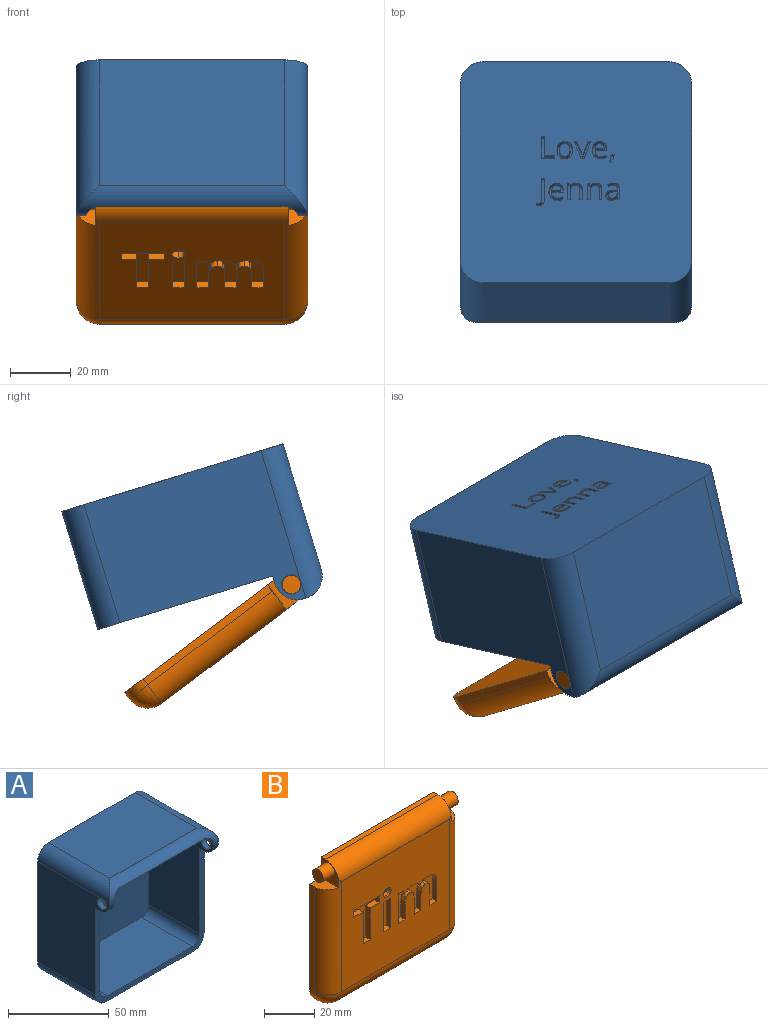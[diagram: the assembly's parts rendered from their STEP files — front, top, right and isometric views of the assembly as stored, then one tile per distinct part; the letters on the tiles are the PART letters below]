
ASSEMBLY  parts=2 mates=1
PART A: 195 faces, bbox 76.2x50.8x76.2 mm
  f0: plane 76.2x76.2mm, normal (0,1,0), area 5627.7mm2, adj f2,f6,f10,f11,f19,f21,f22,f23
  f1: plane 3.22x0.71mm, normal (0,-1,0), area 2.3mm2, adj f2,f3,f17,f20,f29
  f2: plane 60.96x50.8mm, normal (1,0,0), area 2517.9mm2, adj f0,f1,f12,f14,f16,f17,f19,f23
  f3: plane 59.69x45.72mm, normal (-1,0,0), area 2158mm2, adj f1,f8,f12,f14,f16,f17,f28,f29
  f4: plane 59.69x35.56mm, normal (0,0,1), area 2122.6mm2, adj f8,f16,f27,f28
  f5: plane 3.22x0.71mm, normal (0,-1,0), area 2.3mm2, adj f6,f7,f18,f20,f24
  f6: plane 60.96x50.8mm, normal (-1,0,0), area 2517.9mm2, adj f0,f5,f13,f15,f16,f18,f21,f22
  f7: plane 59.69x45.72mm, normal (1,0,0), area 2158mm2, adj f5,f8,f13,f15,f16,f18,f24,f26
  f8: plane 69.85x69.85mm, normal (0,-1,0), area 4856.9mm2, adj f3,f4,f7,f9,f26,f27,f28,f31
  f9: plane 59.75x44.29mm, normal (0,0,-1), area 2643.7mm2, adj f8,f20,f24,f25,f26,f29,f30,f31
  f10: plane 60.96x40.64mm, normal (0,0,-1), area 2477.4mm2, adj f0,f16,f22,f23
  f11: plane 60.96x43.18mm, normal (0,0,1), area 2632.3mm2, adj f0,f19,f20,f21
  f12: cylinder r=3.17mm len=6.35mm, axis (1,0,0), area 63.3mm2, adj f2,f3,f30
  f13: cylinder r=3.17mm len=6.35mm, axis (-1,0,0), area 63.3mm2, adj f6,f7,f25
  f14: plane 3.18x2.54mm, normal (0,0,-1), area 8.1mm2, adj f2,f3,f16,f17
  f15: plane 3.18x2.54mm, normal (0,0,-1), area 8.1mm2, adj f6,f7,f16,f18
  f16: plane 76.2x60.25mm, normal (0,-1,0), area 590.5mm2, adj f2,f3,f4,f6,f7,f10,f14,f15
  f17: cylinder r=7.62mm len=7.62mm, axis (1,0,0), area 38mm2, adj f1,f2,f3,f14
  f18: cylinder r=7.62mm len=7.62mm, axis (1,0,0), area 38mm2, adj f5,f6,f7,f15
  f19: cylinder r=7.62mm len=50.8mm, axis (0,-1,0), area 574.9mm2, adj f0,f2,f11,f20
  f20: cylinder r=7.62mm len=76.2mm, axis (1,0,0), area 526.7mm2, adj f1,f5,f9,f11,f19,f21,f24,f29
  f21: cylinder r=7.62mm len=50.8mm, axis (0,-1,0), area 574.9mm2, adj f0,f6,f11,f20
  f22: cylinder r=7.62mm len=40.64mm, axis (0,1,0), area 486.4mm2, adj f0,f6,f10,f16
  f23: cylinder r=7.62mm len=40.64mm, axis (0,1,0), area 486.4mm2, adj f0,f2,f10,f16
  f24: cylinder r=5.08mm len=5.08mm, axis (0,1,0), area 26.1mm2, adj f5,f7,f9,f20,f25
  f25: bspline ~5.08x5.08mm, area 27.4mm2, adj f9,f13,f24,f26
  f26: cylinder r=5.08mm len=38.19mm, axis (0,1,0), area 304.7mm2, adj f7,f8,f9,f25
  f27: cylinder r=5.08mm len=35.56mm, axis (0,-1,0), area 283.8mm2, adj f4,f7,f8,f16
  f28: cylinder r=5.08mm len=35.56mm, axis (0,-1,0), area 283.8mm2, adj f3,f4,f8,f16
  f29: cylinder r=5.08mm len=5.08mm, axis (0,1,0), area 26.1mm2, adj f1,f3,f9,f20,f30
  f30: bspline ~5.08x5.08mm, area 27.4mm2, adj f9,f12,f29,f31
  f31: cylinder r=5.08mm len=38.19mm, axis (0,1,0), area 304.7mm2, adj f3,f8,f9,f30
  f32: plane 7.54x2.54mm, normal (1,0,0), area 19.1mm2, adj f0,f33,f37,f38
  f33: plane 4.2x2.54mm, normal (0,0,-1), area 10.7mm2, adj f0,f32,f34,f38
  f34: plane 2.54x0.79mm, normal (-1,0,0), area 2mm2, adj f0,f33,f35,f38
  f35: plane 3.33x2.54mm, normal (0,0,1), area 8.4mm2, adj f0,f34,f36,f38
  f36: plane 6.74x2.54mm, normal (-1,0,0), area 17.1mm2, adj f0,f35,f37,f38
  f37: plane 2.54x0.88mm, normal (0,0,1), area 2.2mm2, adj f0,f32,f36,f38
  f38: plane 7.54x4.2mm, normal (0,1,0), area 9.2mm2, adj f32,f33,f34,f35,f36,f37
  f39: extruded ~2.54x1.26mm, area 3.5mm2, adj f40,f65,f66,f191
  f40: extruded ~2.54x0.79mm, area 2.1mm2, adj f39,f41,f66,f191
  f41: extruded ~2.54x0.71mm, area 2mm2, adj f40,f42,f66,f191
  f42: extruded ~2.54x0.87mm, area 2.6mm2, adj f41,f43,f66,f191
  f43: extruded ~2.54x1.47mm, area 3.9mm2, adj f42,f44,f66,f191
  f44: plane 2.54x0.86mm, normal (-0.04,0,-1), area 2.2mm2, adj f43,f45,f66,f191
  f45: plane 2.54x0.51mm, normal (1,0,0), area 1.3mm2, adj f44,f65,f66,f191
  f46: plane 2.54x0.81mm, normal (0.98,0,-0.21), area 2.1mm2, adj f0,f47,f64,f66
  f47: plane 2.54x0.64mm, normal (0,0,-1), area 1.6mm2, adj f0,f46,f48,f66
  f48: plane 3.86x2.54mm, normal (-1,0,0), area 9.8mm2, adj f0,f47,f49,f66
  f49: extruded ~2.54x1.44mm, area 4mm2, adj f0,f48,f50,f66
  f50: extruded ~2.54x1.5mm, area 4.1mm2, adj f0,f49,f51,f66
  f51: extruded ~2.54x1mm, area 2.6mm2, adj f0,f50,f52,f66
  f52: extruded ~2.54x0.91mm, area 2.5mm2, adj f0,f51,f53,f66
  f53: plane 2.54x0.65mm, normal (0.93,0,-0.37), area 1.8mm2, adj f0,f52,f54,f66
  f54: extruded ~2.54x1.6mm, area 4.2mm2, adj f0,f53,f55,f66
  f55: extruded ~2.54x0.92mm, area 2.5mm2, adj f0,f54,f56,f66
  f56: extruded ~2.54x0.98mm, area 2.7mm2, adj f0,f55,f57,f66
  f57: plane 2.54x0.35mm, normal (1,0,0), area 0.9mm2, adj f0,f56,f58,f66
  f58: plane 2.54x0.96mm, normal (0.03,0,1), area 2.4mm2, adj f0,f57,f59,f66
  f59: extruded ~2.74x2.54mm, area 9.3mm2, adj f0,f58,f60,f66
  f60: extruded ~2.54x1.23mm, area 3.5mm2, adj f0,f59,f61,f66
  f61: extruded ~2.54x1.32mm, area 3.6mm2, adj f0,f60,f62,f66
  f62: extruded ~2.54x1.05mm, area 2.7mm2, adj f0,f61,f63,f66
  f63: extruded ~2.54x0.84mm, area 2.8mm2, adj f0,f62,f64,f66
  f64: plane 2.54x0.04mm, normal (0,0,-1), area 0.1mm2, adj f0,f46,f63,f66
  f65: extruded ~2.54x1.23mm, area 3.4mm2, adj f39,f45,f66,f191
  f66: plane 5.85x4.53mm, normal (0,1,0), area 12.5mm2, adj f39,f40,f41,f42,f43,f44,f45,f46
  f67: plane 5.65x2.54mm, normal (0.93,0,-0.35), area 15.3mm2, adj f0,f68,f76,f77
  f68: plane 2.54x1mm, normal (0,0,-1), area 2.5mm2, adj f0,f67,f69,f77
  f69: plane 5.65x2.54mm, normal (-0.93,0,-0.35), area 15.3mm2, adj f0,f68,f70,f77
  f70: plane 2.54x0.92mm, normal (0,0,1), area 2.3mm2, adj f0,f69,f71,f77
  f71: extruded ~3.75x2.54mm, area 10.1mm2, adj f0,f70,f72,f77
  f72: extruded ~2.54x1.13mm, area 3mm2, adj f0,f71,f73,f77
  f73: plane 2.54x0.04mm, normal (0,0,1), area 0.1mm2, adj f0,f72,f74,f77
  f74: extruded ~2.54x1.53mm, area 4.1mm2, adj f0,f73,f75,f77
  f75: plane 3.35x2.54mm, normal (-0.94,0,0.34), area 9.1mm2, adj f0,f74,f76,f77
  f76: plane 2.54x0.92mm, normal (0,0,1), area 2.3mm2, adj f0,f67,f75,f77
  f77: plane 5.65x5.29mm, normal (0,1,0), area 9.5mm2, adj f67,f68,f69,f70,f71,f72,f73,f74
  f78: plane 2.54x0.12mm, normal (-0.84,0,0.55), area 0.4mm2, adj f0,f79,f84,f85
  f79: plane 2.54x0.94mm, normal (0,0,1), area 2.4mm2, adj f0,f78,f80,f85
  f80: extruded ~2.54x1.26mm, area 3.3mm2, adj f0,f79,f81,f85
  f81: extruded ~2.54x1.32mm, area 3.5mm2, adj f0,f80,f82,f85
  f82: plane 2.54x0.65mm, normal (0,0,-1), area 1.6mm2, adj f0,f81,f83,f85
  f83: extruded ~2.54x1.27mm, area 3.5mm2, adj f0,f82,f84,f85
  f84: extruded ~2.54x1.2mm, area 3.2mm2, adj f0,f78,f83,f85
  f85: plane 2.59x1.56mm, normal (0,1,0), area 2.2mm2, adj f78,f79,f80,f81,f82,f83,f84
  f86: extruded ~2.54x0.76mm, area 2mm2, adj f0,f87,f95,f96
  f87: extruded ~2.54x1.42mm, area 4mm2, adj f0,f86,f88,f96
  f88: extruded ~2.54x1.52mm, area 4.2mm2, adj f0,f87,f89,f96
  f89: plane 7.46x2.54mm, normal (-1,0,0), area 19mm2, adj f0,f88,f90,f96
  f90: plane 2.54x0.88mm, normal (0,0,1), area 2.2mm2, adj f0,f89,f91,f96
  f91: plane 7.54x2.54mm, normal (1,0,0), area 19.1mm2, adj f0,f90,f92,f96
  f92: extruded ~2.54x0.89mm, area 2.4mm2, adj f0,f91,f93,f96
  f93: extruded ~2.54x0.78mm, area 2.2mm2, adj f0,f92,f94,f96
  f94: extruded ~2.54x0.76mm, area 2mm2, adj f0,f93,f95,f96
  f95: plane 2.54x0.75mm, normal (1,0,0), area 1.9mm2, adj f0,f86,f94,f96
  f96: plane 9.52x2.68mm, normal (0,1,0), area 9.3mm2, adj f86,f87,f88,f89,f90,f91,f92,f93
  f97: plane 3.66x2.54mm, normal (1,0,0), area 9.3mm2, adj f0,f98,f113,f114
  f98: plane 2.54x0.86mm, normal (0,0,-1), area 2.2mm2, adj f0,f97,f99,f114
  f99: plane 3.68x2.54mm, normal (-1,0,0), area 9.4mm2, adj f0,f98,f100,f114
  f100: extruded ~2.54x1.58mm, area 4.3mm2, adj f0,f99,f101,f114
  f101: extruded ~2.54x1.54mm, area 4.2mm2, adj f0,f100,f102,f114
  f102: extruded ~2.54x1.06mm, area 2.8mm2, adj f0,f101,f103,f114
  f103: extruded ~2.54x0.74mm, area 2.5mm2, adj f0,f102,f104,f114
  f104: plane 2.54x0.04mm, normal (0,0,1), area 0.1mm2, adj f0,f103,f105,f114
  f105: plane 2.54x0.77mm, normal (-0.98,0,0.18), area 2mm2, adj f0,f104,f106,f114
  f106: plane 2.54x0.7mm, normal (0,0,1), area 1.8mm2, adj f0,f105,f107,f114
  f107: plane 5.65x2.54mm, normal (1,0,0), area 14.3mm2, adj f0,f106,f108,f114
  f108: plane 2.54x0.86mm, normal (0,0,-1), area 2.2mm2, adj f0,f107,f109,f114
  f109: plane 2.96x2.54mm, normal (-1,0,0), area 7.5mm2, adj f0,f108,f110,f114
  f110: extruded ~2.54x1.58mm, area 4.2mm2, adj f0,f109,f111,f114
  f111: extruded ~2.54x1.3mm, area 3.6mm2, adj f0,f110,f112,f114
  f112: extruded ~2.54x0.99mm, area 2.7mm2, adj f0,f111,f113,f114
  f113: extruded ~2.54x1.03mm, area 2.8mm2, adj f0,f97,f112,f114
  f114: plane 5.75x4.72mm, normal (0,1,0), area 11.6mm2, adj f97,f98,f99,f100,f101,f102,f103,f104
  f115: extruded ~2.54x1.08mm, area 3.1mm2, adj f116,f133,f134,f192
  f116: extruded ~2.54x1.03mm, area 2.9mm2, adj f115,f117,f134,f192
  f117: extruded ~2.54x1.24mm, area 3.3mm2, adj f116,f118,f134,f192
  f118: plane 2.95x2.54mm, normal (0,0,1), area 7.5mm2, adj f117,f133,f134,f192
  f119: extruded ~2.54x1.98mm, area 5.5mm2, adj f0,f120,f132,f134
  f120: extruded ~2.54x0.98mm, area 2.5mm2, adj f0,f119,f121,f134
  f121: extruded ~2.54x0.86mm, area 2.3mm2, adj f0,f120,f122,f134
  f122: plane 2.54x0.76mm, normal (-1,0,0), area 1.9mm2, adj f0,f121,f123,f134
  f123: extruded ~2.54x1.8mm, area 4.7mm2, adj f0,f122,f124,f134
  f124: extruded ~2.54x1.34mm, area 3.8mm2, adj f0,f123,f125,f134
  f125: extruded ~2.54x1.51mm, area 4.1mm2, adj f0,f124,f126,f134
  f126: plane 3.89x2.54mm, normal (0,0,-1), area 9.9mm2, adj f0,f125,f127,f134
  f127: plane 2.54x0.54mm, normal (-1,0,0), area 1.4mm2, adj f0,f126,f128,f134
  f128: extruded ~2.54x1.84mm, area 5.1mm2, adj f0,f127,f129,f134
  f129: extruded ~2.54x1.68mm, area 4.8mm2, adj f0,f128,f130,f134
  f130: extruded ~2.54x1.81mm, area 5.2mm2, adj f0,f129,f131,f134
  f131: extruded ~2.54x2.17mm, area 5.9mm2, adj f0,f130,f132,f134
  f132: extruded ~2.54x2.12mm, area 5.8mm2, adj f0,f119,f131,f134
  f133: extruded ~2.54x1.23mm, area 3.4mm2, adj f115,f118,f134,f192
  f134: plane 5.86x4.78mm, normal (0,1,0), area 12.7mm2, adj f115,f116,f117,f118,f119,f120,f121,f122
  f135: extruded ~2.54x1.08mm, area 3.1mm2, adj f136,f153,f154,f193
  f136: extruded ~2.54x1.03mm, area 2.9mm2, adj f135,f137,f154,f193
  f137: extruded ~2.54x1.24mm, area 3.3mm2, adj f136,f138,f154,f193
  f138: plane 2.95x2.54mm, normal (0,0,1), area 7.5mm2, adj f137,f153,f154,f193
  f139: extruded ~2.54x1.98mm, area 5.5mm2, adj f0,f140,f152,f154
  f140: extruded ~2.54x0.98mm, area 2.5mm2, adj f0,f139,f141,f154
  f141: extruded ~2.54x0.86mm, area 2.3mm2, adj f0,f140,f142,f154
  f142: plane 2.54x0.76mm, normal (-1,0,0), area 1.9mm2, adj f0,f141,f143,f154
  f143: extruded ~2.54x1.8mm, area 4.7mm2, adj f0,f142,f144,f154
  f144: extruded ~2.54x1.34mm, area 3.8mm2, adj f0,f143,f145,f154
  f145: extruded ~2.54x1.51mm, area 4.1mm2, adj f0,f144,f146,f154
  f146: plane 3.89x2.54mm, normal (0,0,-1), area 9.9mm2, adj f0,f145,f147,f154
  f147: plane 2.54x0.54mm, normal (-1,0,0), area 1.4mm2, adj f0,f146,f148,f154
  f148: extruded ~2.54x1.84mm, area 5.1mm2, adj f0,f147,f149,f154
  f149: extruded ~2.54x1.68mm, area 4.8mm2, adj f0,f148,f150,f154
  f150: extruded ~2.54x1.81mm, area 5.2mm2, adj f0,f149,f151,f154
  f151: extruded ~2.54x2.17mm, area 5.9mm2, adj f0,f150,f152,f154
  f152: extruded ~2.54x2.12mm, area 5.8mm2, adj f0,f139,f151,f154
  f153: extruded ~2.54x1.23mm, area 3.4mm2, adj f135,f138,f154,f193
  f154: plane 5.86x4.78mm, normal (0,1,0), area 12.7mm2, adj f135,f136,f137,f138,f139,f140,f141,f142
  f155: extruded ~2.54x1.65mm, area 4.4mm2, adj f156,f171,f172,f194
  f156: extruded ~2.54x1.64mm, area 4.4mm2, adj f155,f157,f172,f194
  f157: extruded ~2.54x1.27mm, area 3.6mm2, adj f156,f158,f172,f194
  f158: extruded ~2.54x1.29mm, area 3.7mm2, adj f157,f159,f172,f194
  f159: extruded ~2.54x1.64mm, area 4.4mm2, adj f158,f160,f172,f194
  f160: extruded ~2.54x1.65mm, area 4.4mm2, adj f159,f161,f172,f194
  f161: extruded ~2.54x1.28mm, area 3.7mm2, adj f160,f171,f172,f194
  f162: extruded ~2.54x2.16mm, area 5.9mm2, adj f0,f163,f170,f172
  f163: extruded ~2.54x2.13mm, area 5.8mm2, adj f0,f162,f164,f172
  f164: extruded ~2.54x1.88mm, area 5.4mm2, adj f0,f163,f165,f172
  f165: extruded ~2.54x1.92mm, area 5.4mm2, adj f0,f164,f166,f172
  f166: extruded ~2.54x2.15mm, area 5.9mm2, adj f0,f165,f167,f172
  f167: extruded ~2.54x1.56mm, area 4.1mm2, adj f0,f166,f168,f172
  f168: extruded ~2.54x1.02mm, area 3.5mm2, adj f0,f167,f169,f172
  f169: extruded ~2.54x1.35mm, area 3.6mm2, adj f0,f168,f170,f172
  f170: extruded ~2.54x1.92mm, area 5.4mm2, adj f0,f162,f169,f172
  f171: extruded ~2.54x1.27mm, area 3.7mm2, adj f155,f161,f172,f194
  f172: plane 5.86x5.19mm, normal (0,1,0), area 12.3mm2, adj f155,f156,f157,f158,f159,f160,f161,f162
  f173: plane 3.66x2.54mm, normal (1,0,0), area 9.3mm2, adj f0,f174,f189,f190
  f174: plane 2.54x0.86mm, normal (0,0,-1), area 2.2mm2, adj f0,f173,f175,f190
  f175: plane 3.68x2.54mm, normal (-1,0,0), area 9.4mm2, adj f0,f174,f176,f190
  f176: extruded ~2.54x1.58mm, area 4.3mm2, adj f0,f175,f177,f190
  f177: extruded ~2.54x1.54mm, area 4.2mm2, adj f0,f176,f178,f190
  f178: extruded ~2.54x1.06mm, area 2.8mm2, adj f0,f177,f179,f190
  f179: extruded ~2.54x0.74mm, area 2.5mm2, adj f0,f178,f180,f190
  f180: plane 2.54x0.04mm, normal (0,0,1), area 0.1mm2, adj f0,f179,f181,f190
  f181: plane 2.54x0.77mm, normal (-0.98,0,0.18), area 2mm2, adj f0,f180,f182,f190
  f182: plane 2.54x0.7mm, normal (0,0,1), area 1.8mm2, adj f0,f181,f183,f190
  f183: plane 5.65x2.54mm, normal (1,0,0), area 14.3mm2, adj f0,f182,f184,f190
  f184: plane 2.54x0.86mm, normal (0,0,-1), area 2.2mm2, adj f0,f183,f185,f190
  f185: plane 2.96x2.54mm, normal (-1,0,0), area 7.5mm2, adj f0,f184,f186,f190
  f186: extruded ~2.54x1.58mm, area 4.2mm2, adj f0,f185,f187,f190
  f187: extruded ~2.54x1.3mm, area 3.6mm2, adj f0,f186,f188,f190
  f188: extruded ~2.54x0.99mm, area 2.7mm2, adj f0,f187,f189,f190
  f189: extruded ~2.54x1.03mm, area 2.8mm2, adj f0,f173,f188,f190
  f190: plane 5.75x4.72mm, normal (0,1,0), area 11.6mm2, adj f173,f174,f175,f176,f177,f178,f179,f180
  f191: plane 2.78x2.17mm, normal (0,1,0), area 4.9mm2, adj f39,f40,f41,f42,f43,f44,f45,f65
  f192: plane 2.95x1.67mm, normal (0,1,0), area 4mm2, adj f115,f116,f117,f118,f133
  f193: plane 2.95x1.67mm, normal (0,1,0), area 4mm2, adj f135,f136,f137,f138,f153
  f194: plane 4.41x3.42mm, normal (0,1,0), area 12.5mm2, adj f155,f156,f157,f158,f159,f160,f161,f171
PART B: 71 faces, bbox 76.2x10.2x69.1 mm
  f0: plane 60.96x53.9mm, normal (0,-1,0), area 2907.1mm2, adj f14,f16,f18,f19,f22,f23,f24,f25
  f1: plane 51.36x2.54mm, normal (1,0,0), area 130.5mm2, adj f2,f4,f14,f15
  f2: plane 10.05x6.35mm, normal (0,0,1), area 52.1mm2, adj f1,f3,f4,f14
  f3: plane 10.16x10.05mm, normal (1,0,0), area 61.2mm2, adj f2,f4,f6,f7,f14,f16
  f4: plane 76.2x69.14mm, normal (0,1,0), area 5114.4mm2, adj f1,f2,f3,f5,f6,f9,f10,f11
  f5: plane 60.96x2.54mm, normal (0,0,-1), area 154.8mm2, adj f4,f15,f19,f21
  f6: plane 63.5x2.54mm, normal (0,0,1), area 161.3mm2, adj f3,f4,f11,f16
  f7: cylinder r=3.05mm len=6.35mm, axis (-1,0,0), area 121.6mm2, adj f3,f8
  f8: plane 6.1x6.1mm, normal (1,0,0), area 29.2mm2, adj f7
  f9: plane 51.36x2.54mm, normal (-1,0,0), area 130.5mm2, adj f4,f10,f18,f21
  f10: plane 10.05x6.35mm, normal (0,0,1), area 52.1mm2, adj f4,f9,f11,f18
  f11: plane 10.16x10.05mm, normal (-1,0,0), area 61.2mm2, adj f4,f6,f10,f12,f16,f18
  f12: cylinder r=3.05mm len=6.35mm, axis (1,0,0), area 121.6mm2, adj f11,f13
  f13: plane 6.1x6.1mm, normal (-1,0,0), area 29.2mm2, adj f12
  f14: cylinder r=7.62mm len=55.17mm, axis (0,0,-1), area 618.8mm2, adj f0,f1,f2,f3,f16,f17
  f15: cylinder r=7.62mm len=7.62mm, axis (0,1,0), area 30.4mm2, adj f1,f4,f5,f17
  f16: cylinder r=7.62mm len=63.5mm, axis (1,0,0), area 758.4mm2, adj f0,f3,f6,f11,f14,f18
  f17: sphere r=7.62mm, area 91.2mm2, adj f14,f15,f19
  f18: cylinder r=7.62mm len=55.17mm, axis (0,0,-1), area 618.8mm2, adj f0,f9,f10,f11,f16,f20
  f19: cylinder r=7.62mm len=60.96mm, axis (-1,0,0), area 729.7mm2, adj f0,f5,f17,f20
  f20: sphere r=7.62mm, area 91.2mm2, adj f18,f19,f21
  f21: cylinder r=7.62mm len=7.62mm, axis (0,1,0), area 30.4mm2, adj f4,f5,f9,f20
  f22: plane 3.94x2.54mm, normal (0,0,1), area 10mm2, adj f0,f23,f25,f26
  f23: plane 14.44x2.54mm, normal (-1,0,0), area 36.7mm2, adj f0,f22,f24,f26
  f24: plane 3.94x2.54mm, normal (0,0,-1), area 10mm2, adj f0,f23,f25,f26
  f25: plane 14.44x2.54mm, normal (1,0,0), area 36.7mm2, adj f0,f22,f24,f26
  f26: plane 14.44x3.94mm, normal (0,-1,0), area 56.9mm2, adj f22,f23,f24,f25
  f27: extruded ~2.54x2.15mm, area 8.4mm2, adj f0,f28,f31,f32
  f28: extruded ~2.54x2.15mm, area 8.4mm2, adj f0,f27,f29,f32
  f29: extruded ~2.54x1.61mm, area 4.4mm2, adj f0,f28,f30,f32
  f30: extruded ~2.54x1.43mm, area 4mm2, adj f0,f29,f31,f32
  f31: extruded ~2.54x2.15mm, area 8.4mm2, adj f0,f27,f30,f32
  f32: plane 4.29x3.87mm, normal (0,-1,0), area 13.8mm2, adj f27,f28,f29,f30,f31
  f33: plane 4.01x2.54mm, normal (0,0,1), area 10.2mm2, adj f0,f34,f40,f41
  f34: plane 15.56x2.54mm, normal (-1,0,0), area 39.5mm2, adj f0,f33,f35,f41
  f35: plane 5.13x2.54mm, normal (0,0,1), area 13mm2, adj f0,f34,f36,f41
  f36: plane 3.33x2.54mm, normal (-1,0,0), area 8.5mm2, adj f0,f35,f37,f41
  f37: plane 14.26x2.54mm, normal (0,0,-1), area 36.2mm2, adj f0,f36,f38,f41
  f38: plane 3.33x2.54mm, normal (1,0,0), area 8.5mm2, adj f0,f37,f39,f41
  f39: plane 5.13x2.54mm, normal (0,0,1), area 13mm2, adj f0,f38,f40,f41
  f40: plane 15.56x2.54mm, normal (1,0,0), area 39.5mm2, adj f0,f33,f39,f41
  f41: plane 18.89x14.26mm, normal (0,-1,0), area 109.8mm2, adj f33,f34,f35,f36,f37,f38,f39,f40
  f42: plane 3.94x2.54mm, normal (0,0,1), area 10mm2, adj f0,f43,f69,f70
  f43: plane 7.25x2.54mm, normal (-1,0,0), area 18.4mm2, adj f0,f42,f44,f70
  f44: extruded ~3.28x2.54mm, area 8.7mm2, adj f0,f43,f45,f70
  f45: extruded ~2.54x2.16mm, area 6.4mm2, adj f0,f44,f46,f70
  f46: extruded ~2.54x1.65mm, area 4.8mm2, adj f0,f45,f47,f70
  f47: extruded ~2.54x2.34mm, area 6.2mm2, adj f0,f46,f48,f70
  f48: plane 8.44x2.54mm, normal (1,0,0), area 21.4mm2, adj f0,f47,f49,f70
  f49: plane 3.95x2.54mm, normal (0,0,1), area 10mm2, adj f0,f48,f50,f70
  f50: plane 9.42x2.54mm, normal (-1,0,0), area 23.9mm2, adj f0,f49,f51,f70
  f51: extruded ~4.04x2.54mm, area 11mm2, adj f0,f50,f52,f70
  f52: extruded ~3.71x2.54mm, area 10.2mm2, adj f0,f51,f53,f70
  f53: extruded ~2.55x2.54mm, area 6.7mm2, adj f0,f52,f54,f70
  f54: extruded ~2.54x1.71mm, area 6mm2, adj f0,f53,f55,f70
  f55: plane 2.54x0.35mm, normal (0,0,-1), area 0.9mm2, adj f0,f54,f56,f70
  f56: extruded ~4.39x2.54mm, area 13.1mm2, adj f0,f55,f57,f70
  f57: extruded ~2.54x2.52mm, area 6.6mm2, adj f0,f56,f58,f70
  f58: extruded ~2.54x1.68mm, area 5.9mm2, adj f0,f57,f59,f70
  f59: plane 2.54x0.22mm, normal (0,0,-1), area 0.6mm2, adj f0,f58,f60,f70
  f60: plane 2.54x1.85mm, normal (-0.96,0,-0.28), area 4.9mm2, adj f0,f59,f61,f70
  f61: plane 3.01x2.54mm, normal (0,0,-1), area 7.6mm2, adj f0,f60,f62,f70
  f62: plane 14.44x2.54mm, normal (1,0,0), area 36.7mm2, adj f0,f61,f63,f70
  f63: plane 3.94x2.54mm, normal (0,0,1), area 10mm2, adj f0,f62,f64,f70
  f64: plane 6.8x2.54mm, normal (-1,0,0), area 17.3mm2, adj f0,f63,f65,f70
  f65: extruded ~3.65x2.54mm, area 9.5mm2, adj f0,f64,f66,f70
  f66: extruded ~2.54x2.2mm, area 6.6mm2, adj f0,f65,f67,f70
  f67: extruded ~2.54x1.65mm, area 4.8mm2, adj f0,f66,f68,f70
  f68: extruded ~2.54x2.34mm, area 6.2mm2, adj f0,f67,f69,f70
  f69: plane 8.44x2.54mm, normal (1,0,0), area 21.4mm2, adj f0,f42,f68,f70
  f70: plane 21.94x14.71mm, normal (0,-1,0), area 198mm2, adj f42,f43,f44,f45,f46,f47,f48,f49
PLACE A rot(axis=(1,0,0),73deg) t=(-24.06,-211.7,-19.11)mm
PLACE B rot(axis=(1,0,0),53deg) t=(-24.06,-223.61,-69.12)mm
MATE revolute B.f7 <-> A.f12  axis (-1,0,0) through (-62.16,-250.92,-54.25)mm
